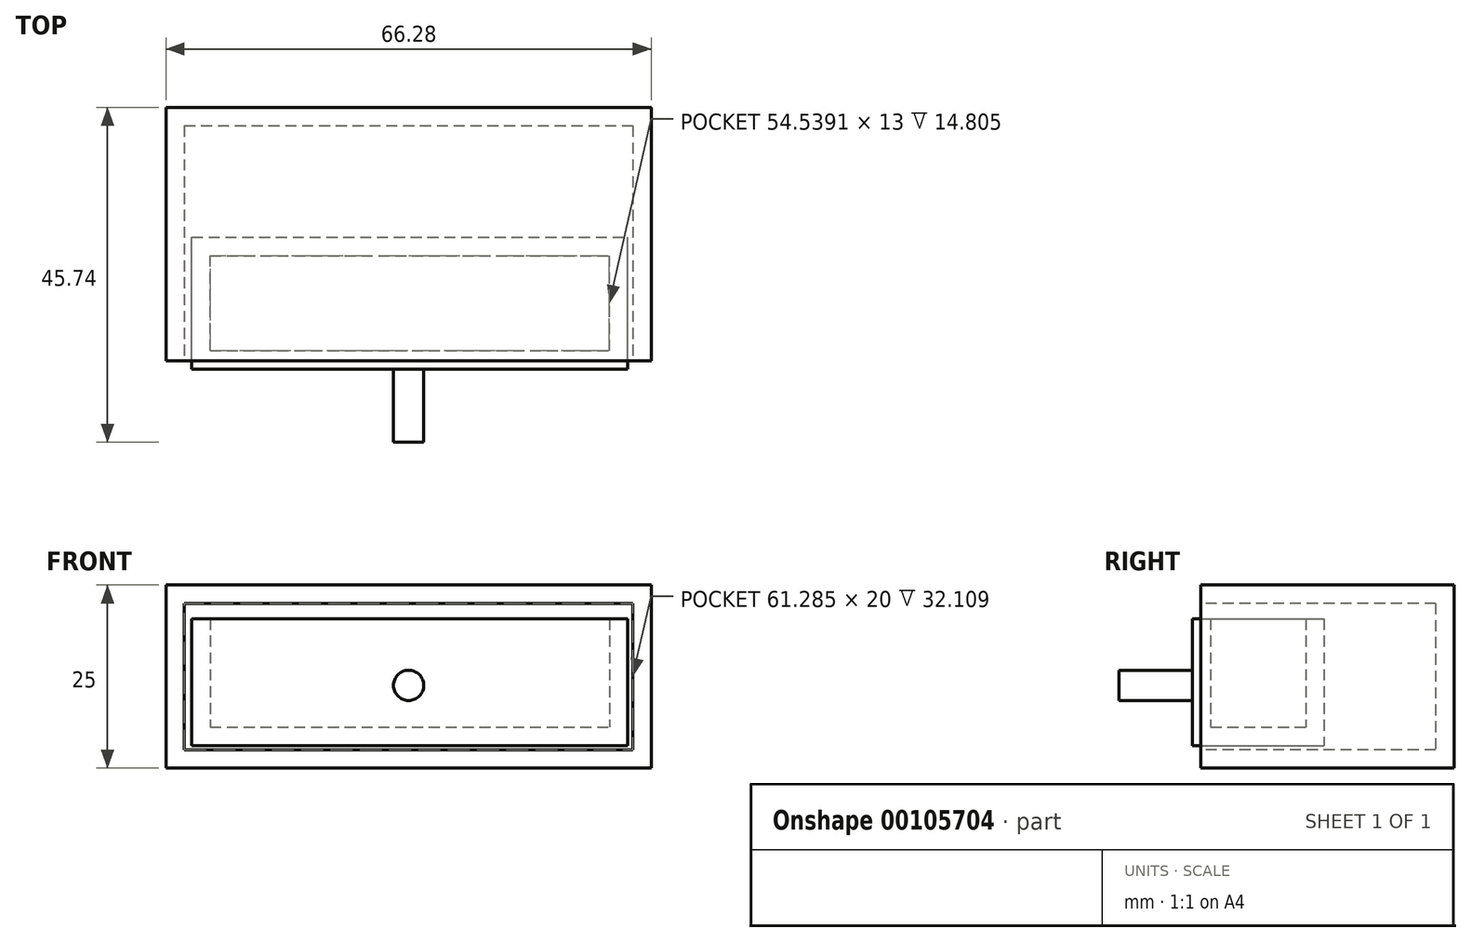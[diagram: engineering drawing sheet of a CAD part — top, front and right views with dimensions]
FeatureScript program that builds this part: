
annotation { "Feature Type Name" : "Feature", "Feature Type Description" : "" }
export const myFeature = defineFeature(function(context is Context, id is Id, definition is map)
    precondition{}
    {
        {
            var Q0;
            Q0=qCreatedBy(makeId("Top.planeOp"),FACE);
            var sketch = newSketch(context, id + "F0", { "sketchPlane" : qUnion([Q0])});
            skLineSegment(sketch, "E0.bottom", {"start": v(-33.14, 17.74) * mm, "end": v(33.14, 17.74) * mm});
            skLineSegment(sketch, "E0.top", {"start": v(-33.14, -16.86) * mm, "end": v(33.14, -16.86) * mm});
            skLineSegment(sketch, "E0.left", {"start": v(-33.14, 17.74) * mm, "end": v(-33.14, -16.86) * mm});
            skLineSegment(sketch, "E0.right", {"start": v(33.14, 17.74) * mm, "end": v(33.14, -16.86) * mm});
            skSolve(sketch);
        }
        {
            var Q0;
            Q0=makeQuery(id+"F0.imprint","IMPRINT",FACE,{"disambiguationData":[TD([[makeQuery(id+"F0.imprint","IMPRINT",EDGE,{"derivedFrom":sQuery(id+"F0.wireOp",EDGE,"E0.bottom")}),-1.0]])]});
            extrude(context, id + "F1", {"entities" : qUnion([Q0]), "depth" : 25 * mm});
        }
        {
            var Q0;
            Q0=makeQuery(id+"F1.opExtrude","SWEPT_FACE",FACE,{"disambiguationData":[OSD([sQuery(id+"F0.wireOp",EDGE,"E0.top")])]});
            shell(context, id + "F2", {"entities" : qUnion([Q0]), "thickness" : 2.5 * mm});
        }
        {
            var Q0;
            Q0=qCreatedBy(makeId("Front.planeOp"),FACE);
            var sketch = newSketch(context, id + "F3", { "sketchPlane" : qUnion([Q0])});
            skLineSegment(sketch, "E1.bottom", {"start": v(-29.62, 20.38) * mm, "end": v(29.92, 20.38) * mm});
            skLineSegment(sketch, "E1.top", {"start": v(-29.62, 3.08) * mm, "end": v(29.92, 3.08) * mm});
            skLineSegment(sketch, "E1.left", {"start": v(-29.62, 20.38) * mm, "end": v(-29.62, 3.08) * mm});
            skLineSegment(sketch, "E1.right", {"start": v(29.92, 20.38) * mm, "end": v(29.92, 3.08) * mm});
            skSolve(sketch);
        }
        {
            var Q0;
            Q0=makeQuery(id+"F3.imprint","IMPRINT",FACE,{"disambiguationData":[TD([[makeQuery(id+"F3.imprint","IMPRINT",EDGE,{"derivedFrom":sQuery(id+"F3.wireOp",EDGE,"E1.bottom")}),-1.0]])]});
            extrude(context, id + "F4", {"entities" : qUnion([Q0]), "depth" : 18 * mm});
        }
        {
            var Q0;
            Q0=makeQuery(id+"F4.opExtrude","SWEPT_FACE",FACE,{"disambiguationData":[OSD([sQuery(id+"F3.wireOp",EDGE,"E1.bottom")])]});
            shell(context, id + "F5", {"entities" : qUnion([Q0]), "thickness" : 2.5 * mm});
        }
        {
            var Q0;
            Q0=makeQuery(id+"F4.opExtrude","CAP_FACE",FACE,{"disambiguationData":[OSD([sQuery(id+"F3.wireOp",EDGE,"E1.bottom"),sQuery(id+"F3.wireOp",EDGE,"E1.top"),sQuery(id+"F3.wireOp",EDGE,"E1.left"),sQuery(id+"F3.wireOp",EDGE,"E1.right")])],"isStart":false});
            var sketch = newSketch(context, id + "F6", { "sketchPlane" : qUnion([Q0])});
            skCircle(sketch, "E2", {"center": v(0, 11.3) * mm, "radius": 2.07 * mm});
            skSolve(sketch);
        }
        {
            var Q0;
            Q0=makeQuery(id+"F6.imprint","IMPRINT",FACE,{"disambiguationData":[TD([[makeQuery(id+"F6.imprint","IMPRINT",EDGE,{"derivedFrom":sQuery(id+"F6.wireOp",EDGE,"E2")}),1.0]])]});
            extrude(context, id + "F7", {"entities" : qUnion([Q0]), "operationType" : NewBodyOperationType.ADD, "depth" : 10 * mm});
        }
        {
            var Q0;
            Q0=makeQuery(id+"F1.opExtrude","CAP_FACE",FACE,{"disambiguationData":[OSD([sQuery(id+"F0.wireOp",EDGE,"E0.bottom"),sQuery(id+"F0.wireOp",EDGE,"E0.top"),sQuery(id+"F0.wireOp",EDGE,"E0.left"),sQuery(id+"F0.wireOp",EDGE,"E0.right")])],"isStart":false});
            var sketch = newSketch(context, id + "F8", { "sketchPlane" : qUnion([Q0])});
            skEllipse(sketch, "E3", {"center": v(0, 0) * mm, "majorRadius": 24.94 * mm, "minorRadius": 11.58 * mm, "majorAxis": v(1, 0)});
            skSolve(sketch);
        }
        {
            var Q0;
            Q0=sQuery(id+"F8.wireOp",EDGE,"E3");
            extrude(context, id + "F9", {"bodyType" : ToolBodyType.SURFACE, "surfaceEntities" : qUnion([Q0]), "depth" : 20 * mm});
        }
    });
